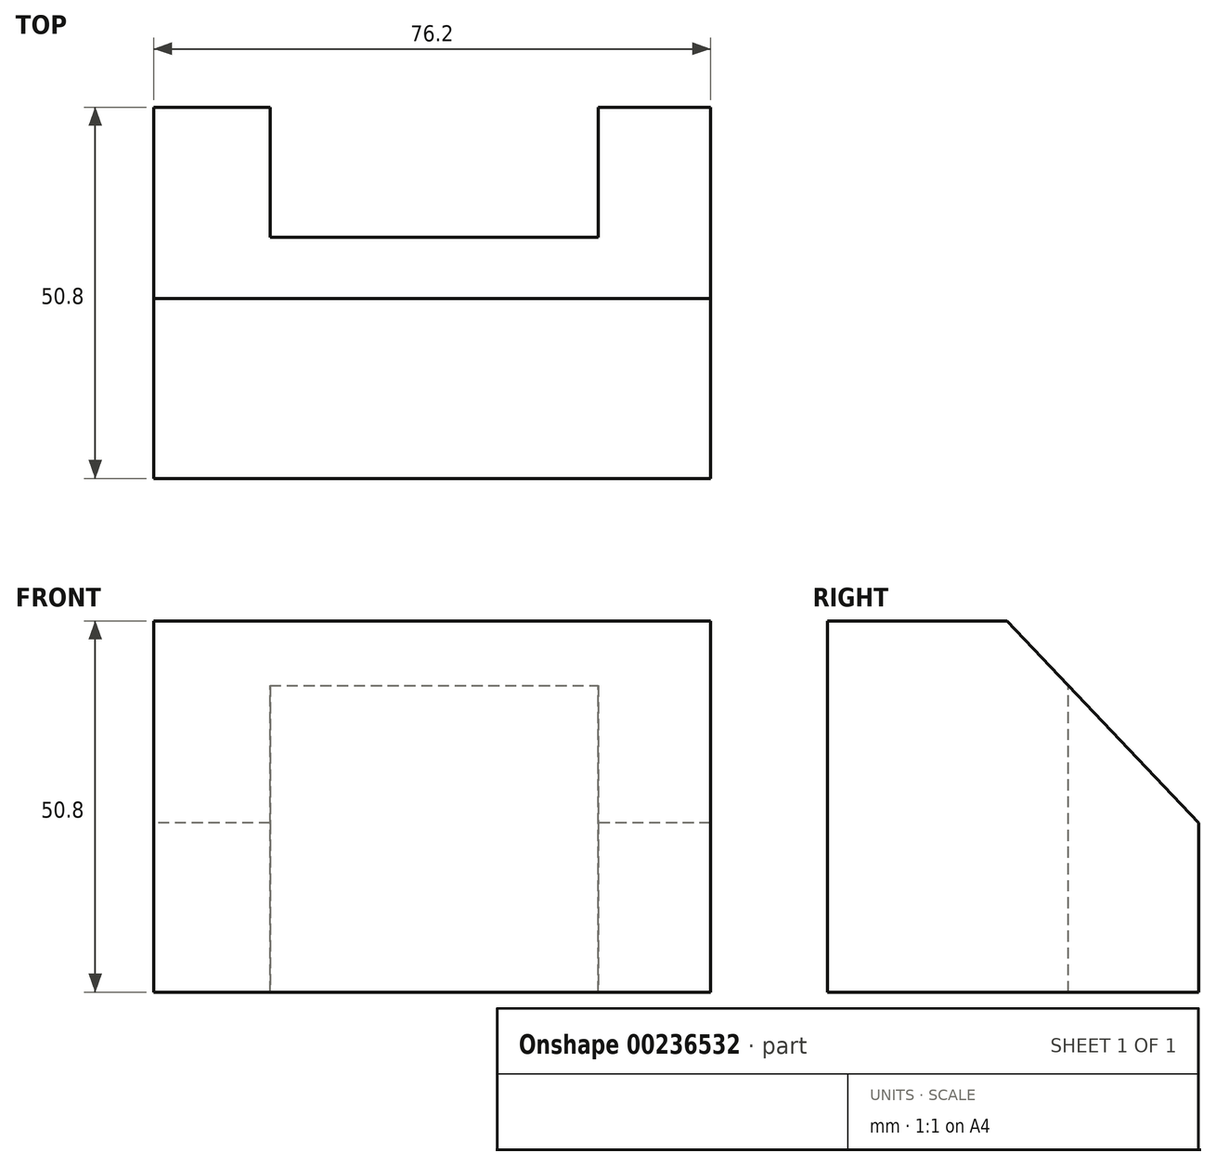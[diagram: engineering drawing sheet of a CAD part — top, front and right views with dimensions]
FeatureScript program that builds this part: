
annotation { "Feature Type Name" : "Feature", "Feature Type Description" : "" }
export const myFeature = defineFeature(function(context is Context, id is Id, definition is map)
    precondition{}
    {
        {
            var Q0;
            Q0=qCreatedBy(makeId("Top.planeOp"),FACE);
            var sketch = newSketch(context, id + "F0", { "sketchPlane" : qUnion([Q0])});
            skLineSegment(sketch, "E0.bottom", {"start": v(-37.33, 17.83) * mm, "end": v(38.87, 17.83) * mm});
            skLineSegment(sketch, "E0.top", {"start": v(-37.33, -32.97) * mm, "end": v(38.87, -32.97) * mm});
            skLineSegment(sketch, "E0.left", {"start": v(-37.33, 17.83) * mm, "end": v(-37.33, -32.97) * mm});
            skLineSegment(sketch, "E0.right", {"start": v(38.87, 17.83) * mm, "end": v(38.87, -32.97) * mm});
            skSolve(sketch);
        }
        {
            var Q0;
            Q0=makeQuery(id+"F0.imprint","IMPRINT",FACE,{"disambiguationData":[TD([[makeQuery(id+"F0.imprint","IMPRINT",EDGE,{"derivedFrom":sQuery(id+"F0.wireOp",EDGE,"E0.bottom")}),-1.0]])]});
            extrude(context, id + "F1", {"entities" : qUnion([Q0]), "depth" : 50.8 * mm});
        }
        {
            var Q0;
            Q0=makeQuery(id+"F1.opExtrude","SWEPT_FACE",FACE,{"disambiguationData":[OSD([sQuery(id+"F0.wireOp",EDGE,"E0.left")])]});
            var sketch = newSketch(context, id + "F2", { "sketchPlane" : qUnion([Q0])});
            skLineSegment(sketch, "E1", {"start": v(8.4, 50.8) * mm, "end": v(-17.83, 23.16) * mm});
            skLineSegment(sketch, "E2", {"start": v(-17.83, 23.16) * mm, "end": v(-17.83, 50.8) * mm});
            skLineSegment(sketch, "E3", {"start": v(-17.83, 50.8) * mm, "end": v(8.4, 50.8) * mm});
            skSolve(sketch);
        }
        {
            var Q0;
            Q0=makeQuery(id+"F2.imprint","IMPRINT",FACE,{"disambiguationData":[TD([[makeQuery(id+"F2.imprint","IMPRINT",EDGE,{"derivedFrom":sQuery(id+"F2.wireOp",EDGE,"E1")}),-1.0]])]});
            extrude(context, id + "F3", {"entities" : qUnion([Q0]), "operationType" : NewBodyOperationType.REMOVE, "oppositeDirection" : true, "depth" : 81.8 * mm});
        }
        {
            var Q0;
            Q0=qCreatedBy(makeId("Front.planeOp"),FACE);
            var sketch = newSketch(context, id + "F4", { "sketchPlane" : qUnion([Q0])});
            skLineSegment(sketch, "E4.bottom", {"start": v(-21.42, 0) * mm, "end": v(23.49, 0) * mm});
            skLineSegment(sketch, "E4.top", {"start": v(-21.42, 51.88) * mm, "end": v(23.49, 51.88) * mm});
            skLineSegment(sketch, "E4.left", {"start": v(-21.42, 0) * mm, "end": v(-21.42, 51.88) * mm});
            skLineSegment(sketch, "E4.right", {"start": v(23.49, 0) * mm, "end": v(23.49, 51.88) * mm});
            skSolve(sketch);
        }
        {
            var Q0;
            Q0=makeQuery(id+"F4.imprint","IMPRINT",FACE,{"disambiguationData":[TD([[makeQuery(id+"F4.imprint","IMPRINT",EDGE,{"derivedFrom":sQuery(id+"F4.wireOp",EDGE,"E4.bottom")}),1.0]])]});
            extrude(context, id + "F5", {"entities" : qUnion([Q0]), "operationType" : NewBodyOperationType.REMOVE, "oppositeDirection" : true, "depth" : 47.24 * mm});
        }
    });
